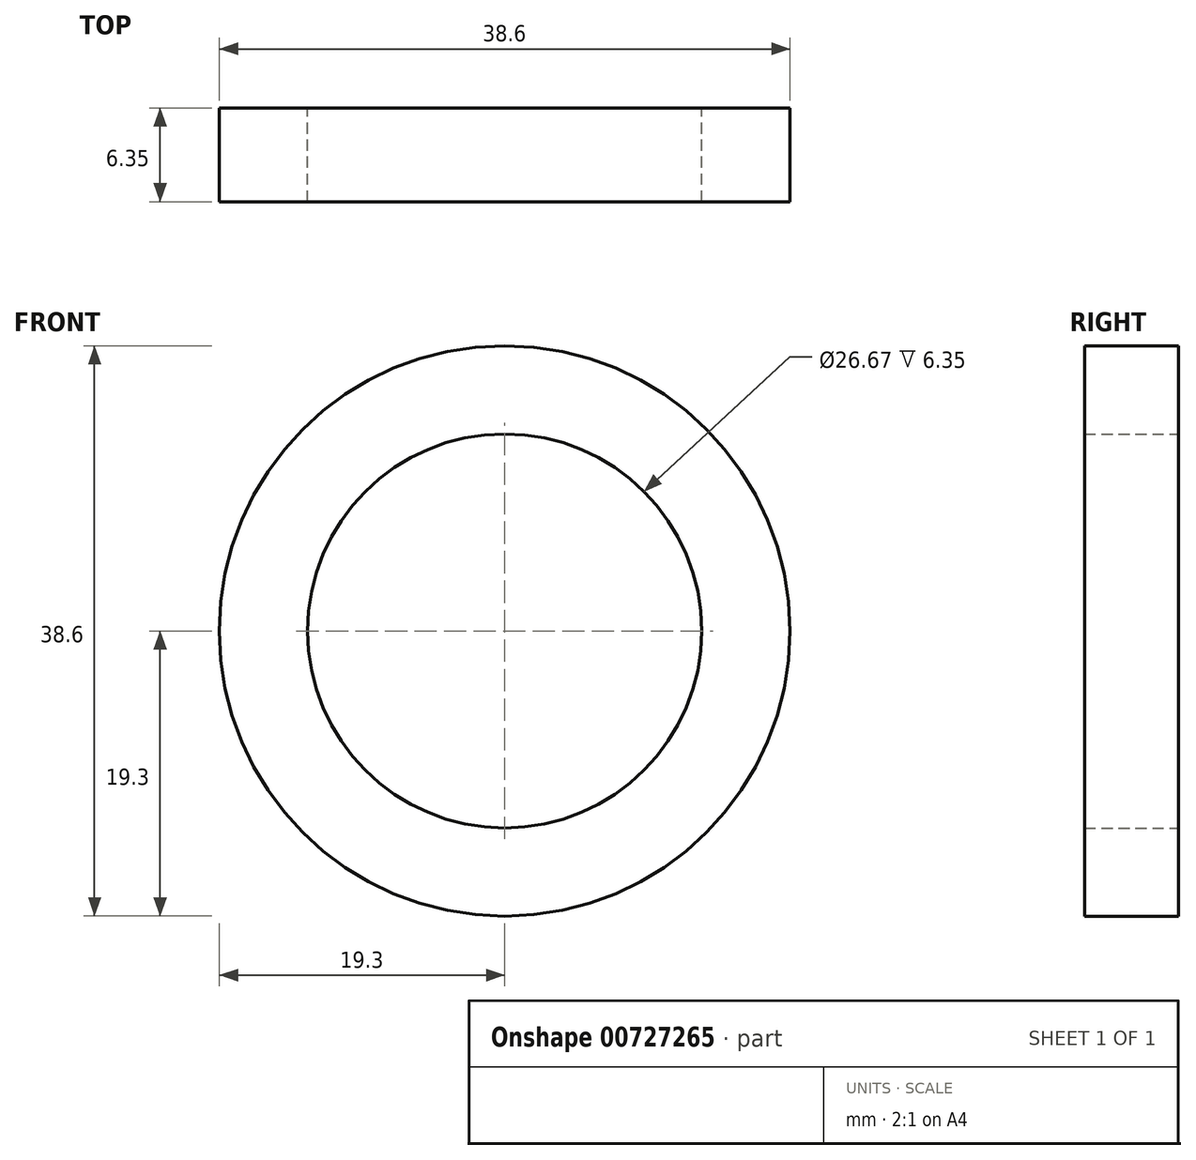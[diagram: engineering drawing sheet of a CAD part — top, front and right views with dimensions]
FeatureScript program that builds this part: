
annotation { "Feature Type Name" : "Feature", "Feature Type Description" : "" }
export const myFeature = defineFeature(function(context is Context, id is Id, definition is map)
    precondition{}
    {
        {
            var Q0;
            Q0=qCreatedBy(makeId("Front.planeOp"),FACE);
            var sketch = newSketch(context, id + "F0", { "sketchPlane" : qUnion([Q0])});
            skCircle(sketch, "E0", {"center": v(0, 0) * mm, "radius": 13.34 * mm});
            skCircle(sketch, "E1", {"center": v(0, 0) * mm, "radius": 19.3 * mm});
            skLineSegment(sketch, "E2", {"start": v(0, 26.53) * mm, "end": v(0, -36.34) * mm, "construction": true});
            skLineSegment(sketch, "E3", {"start": v(31.9, 0) * mm, "end": v(-37.28, 0) * mm, "construction": true});
            skSolve(sketch);
        }
        {
            var Q0;
            Q0=makeQuery(id+"F0.imprint","IMPRINT",FACE,{"disambiguationData":[TD([[makeQuery(id+"F0.imprint","IMPRINT",EDGE,{"derivedFrom":sQuery(id+"F0.wireOp",EDGE,"E0")}),-1.0]])]});
            extrude(context, id + "F1", {"entities" : qUnion([Q0]), "depth" : 6.35 * mm, "offsetDistance" : 25.4 * mm});
        }
    });
